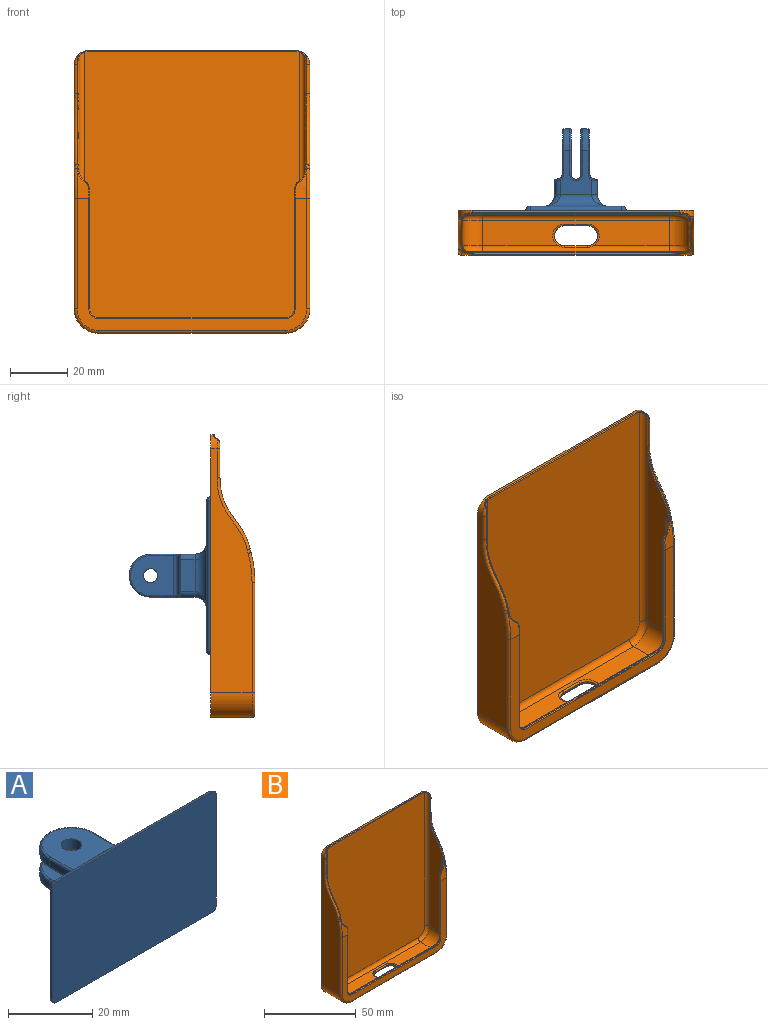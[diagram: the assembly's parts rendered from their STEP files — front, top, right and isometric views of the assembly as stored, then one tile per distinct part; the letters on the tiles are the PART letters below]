
ASSEMBLY  parts=2 mates=1
PART A: 67 faces, bbox 55x29.1x35 mm
  f0: cylinder r=1.68mm len=14mm, axis (1,0,0), area 73.7mm2, adj f13,f14,f51,f54
  f1: cylinder r=7.5mm len=15mm, axis (0,0,-1), area 47.7mm2, adj f3,f4,f43,f50
  f2: cylinder r=2.45mm len=4.9mm, axis (0,0,-1), area 46.6mm2, adj f12,f13
  f3: plane 15.5x11mm, normal (-1,0,0), area 102mm2, adj f1,f5,f26,f30,f36,f39,f41,f49
  f4: plane 15.5x11mm, normal (1,0,0), area 102mm2, adj f1,f5,f27,f32,f34,f45,f47,f52
  f5: cylinder r=7.5mm len=15mm, axis (0,0,-1), area 47.7mm2, adj f3,f4,f55,f65
  f6: cylinder r=2.45mm len=4.9mm, axis (0,0,-1), area 46.6mm2, adj f10,f14
  f7: plane 11x5mm, normal (0,0,-1), area 55mm2, adj f28,f30,f32,f44
  f8: plane 11x5mm, normal (0,0,1), area 55mm2, adj f25,f34,f36,f58
  f9: plane 12.8x0.3mm, normal (0,1,0), area 3.7mm2, adj f38,f57,f58,f60
  f10: plane 15x14mm, normal (0,0,1), area 170.1mm2, adj f6,f38,f63,f65,f66
  f11: plane 12.8x0.3mm, normal (0,1,0), area 3.7mm2, adj f37,f42,f44,f46
  f12: plane 15x14mm, normal (0,0,-1), area 170.1mm2, adj f2,f37,f41,f43,f45
  f13: plane 15.33x14mm, normal (0,0,1), area 174.7mm2, adj f0,f2,f49,f50,f52
  f14: plane 15.33x14mm, normal (0,0,-1), area 174.7mm2, adj f0,f6,f53,f55,f56
  f15: plane 55x35mm, normal (0,-1,0), area 1923.1mm2, adj f17,f18,f19,f20,f21,f22,f23,f24
  f16: plane 52x32mm, normal (0,1,0), area 1135mm2, adj f17,f18,f19,f20,f25,f26,f27,f28
  f17: cylinder r=1.5mm len=52mm, axis (1,0,0), area 122.5mm2, adj f15,f16,f21,f23
  f18: cylinder r=1.5mm len=32mm, axis (0,0,1), area 75.4mm2, adj f15,f16,f21,f22
  f19: cylinder r=1.5mm len=32mm, axis (0,0,-1), area 75.4mm2, adj f15,f16,f23,f24
  f20: cylinder r=1.5mm len=52mm, axis (-1,0,0), area 122.5mm2, adj f15,f16,f22,f24
  f21: sphere r=1.5mm, area 3.5mm2, adj f15,f17,f18
  f22: sphere r=1.5mm, area 3.5mm2, adj f15,f18,f20
  f23: sphere r=1.5mm, area 3.5mm2, adj f15,f17,f19
  f24: sphere r=1.5mm, area 3.5mm2, adj f15,f19,f20
  f25: cylinder r=4mm len=23mm, axis (-1,0,0), area 96.5mm2, adj f8,f16,f33,f35
  f26: cylinder r=4mm len=23mm, axis (0,0,1), area 96.5mm2, adj f3,f16,f29,f35
  f27: cylinder r=4mm len=23mm, axis (0,0,1), area 96.5mm2, adj f4,f16,f31,f33
  f28: cylinder r=4mm len=23mm, axis (1,0,0), area 96.5mm2, adj f7,f16,f29,f31
  f29: bspline ~6x6mm, area 14.5mm2, adj f26,f28,f30
  f30: cylinder r=2mm len=5.31mm, axis (0,1,0), area 15.9mm2, adj f3,f7,f29,f40,f42
  f31: bspline ~6x6mm, area 14.5mm2, adj f27,f28,f32
  f32: cylinder r=2mm len=5.31mm, axis (0,-1,0), area 15.9mm2, adj f4,f7,f31,f46,f48
  f33: bspline ~6x6mm, area 14.5mm2, adj f25,f27,f34
  f34: cylinder r=2mm len=5.31mm, axis (0,1,0), area 15.9mm2, adj f4,f8,f33,f60,f62
  f35: bspline ~6x6mm, area 14.5mm2, adj f25,f26,f36
  f36: cylinder r=2mm len=5.31mm, axis (0,-1,0), area 15.9mm2, adj f3,f8,f35,f57,f59
  f37: cylinder r=2mm len=14mm, axis (-1,0,0), area 43.6mm2, adj f11,f12,f39,f40,f47,f48
  f38: cylinder r=2mm len=14mm, axis (1,0,0), area 43.6mm2, adj f9,f10,f59,f61,f62,f64
  f39: torus R=2.5mm, axis (1,0,0), area 1.8mm2, adj f3,f37,f40,f41
  f40: bspline ~2.29x1.41mm, area 1.2mm2, adj f30,f37,f39,f42
  f41: cylinder r=0.5mm len=8mm, axis (0,1,0), area 6.3mm2, adj f3,f12,f39,f43
  f42: torus R=1.5mm, axis (0,1,0), area 0.9mm2, adj f11,f30,f40,f44
  f43: torus R=7mm, axis (0,0,-1), area 18.1mm2, adj f1,f12,f41,f45
  f44: cylinder r=0.5mm len=11mm, axis (1,0,0), area 8.6mm2, adj f7,f11,f42,f46
  f45: cylinder r=0.5mm len=8mm, axis (0,-1,0), area 6.3mm2, adj f4,f12,f43,f47
  f46: torus R=1.5mm, axis (0,1,0), area 0.9mm2, adj f11,f32,f44,f48
  f47: torus R=2.5mm, axis (-1,0,0), area 1.8mm2, adj f4,f37,f45,f48
  f48: bspline ~2.29x1.41mm, area 1.2mm2, adj f32,f37,f46,f47
  f49: cylinder r=0.5mm len=8.33mm, axis (0,1,0), area 6.5mm2, adj f3,f13,f50,f51
  f50: torus R=7mm, axis (0,0,1), area 18.1mm2, adj f1,f13,f49,f52
  f51: torus R=2.17mm, axis (1,0,0), area 4.6mm2, adj f0,f3,f49,f53
  f52: cylinder r=0.5mm len=8.33mm, axis (0,-1,0), area 6.5mm2, adj f4,f13,f50,f54
  f53: cylinder r=0.5mm len=8.33mm, axis (0,-1,0), area 6.5mm2, adj f3,f14,f51,f55
  f54: torus R=2.17mm, axis (-1,0,0), area 4.6mm2, adj f0,f4,f52,f56
  f55: torus R=7mm, axis (0,0,1), area 18.1mm2, adj f5,f14,f53,f56
  f56: cylinder r=0.5mm len=8.33mm, axis (0,1,0), area 6.5mm2, adj f4,f14,f54,f55
  f57: torus R=1.5mm, axis (0,-1,0), area 0.9mm2, adj f9,f36,f58,f59
  f58: cylinder r=0.5mm len=11mm, axis (1,0,0), area 8.6mm2, adj f8,f9,f57,f60
  f59: bspline ~2.29x1.41mm, area 1.2mm2, adj f36,f38,f57,f61
  f60: torus R=1.5mm, axis (0,-1,0), area 0.9mm2, adj f9,f34,f58,f62
  f61: torus R=2.5mm, axis (1,0,0), area 1.8mm2, adj f3,f38,f59,f63
  f62: bspline ~2.29x1.41mm, area 1.2mm2, adj f34,f38,f60,f64
  f63: cylinder r=0.5mm len=8mm, axis (0,1,0), area 6.3mm2, adj f3,f10,f61,f65
  f64: torus R=2.5mm, axis (-1,0,0), area 1.8mm2, adj f4,f38,f62,f66
  f65: torus R=7mm, axis (0,0,1), area 18.1mm2, adj f5,f10,f63,f66
  f66: cylinder r=0.5mm len=8mm, axis (0,-1,0), area 6.3mm2, adj f4,f10,f64,f65
PART B: 112 faces, bbox 83.6x15.8x99.4 mm
  f0: plane 72.2x0.9mm, normal (0,0,1), area 65mm2, adj f2,f46,f47,f97
  f1: plane 94.7x75mm, normal (0,-1,0), area 7091.6mm2, adj f39,f40,f41,f42,f43,f95,f97,f99
  f2: plane 98.6x82.2mm, normal (0,1,0), area 8062.4mm2, adj f0,f8,f9,f10,f11,f12,f46,f47
  f3: plane 70.95x10.57mm, normal (1,0,0), area 555.3mm2, adj f7,f38,f43,f45,f90,f92,f94
  f4: plane 65x9mm, normal (0,0,1), area 473.1mm2, adj f6,f7,f36,f41,f102,f103,f104
  f5: plane 70.95x10.57mm, normal (-1,0,0), area 555.3mm2, adj f6,f34,f39,f44,f81,f83,f85
  f6: cylinder r=7mm len=9mm, axis (0,1,0), area 99mm2, adj f4,f5,f35,f40
  f7: cylinder r=7mm len=9mm, axis (0,1,0), area 99mm2, adj f3,f4,f37,f42
  f8: plane 85x14.4mm, normal (-1,0,0), area 898.4mm2, adj f2,f9,f46,f49,f50,f51,f52,f53
  f9: cylinder r=8.6mm len=14.4mm, axis (0,1,0), area 194.5mm2, adj f2,f8,f10,f54
  f10: plane 65x14.4mm, normal (0,0,-1), area 817.6mm2, adj f2,f9,f11,f55,f108,f109,f110,f111
  f11: cylinder r=8.6mm len=14.4mm, axis (0,1,0), area 194.5mm2, adj f2,f10,f12,f56
  f12: plane 85x14.4mm, normal (1,0,0), area 898.4mm2, adj f2,f11,f47,f57,f58,f59,f60,f61
  f13: plane 11.57x0.32mm, normal (0,-1,0), area 3.5mm2, adj f14,f61,f62,f89
  f14: extruded ~24.84x10.49mm, area 8.3mm2, adj f13,f30,f60,f85,f87
  f15: plane 11.57x0.32mm, normal (0,-1,0), area 3.5mm2, adj f16,f48,f49,f98
  f16: extruded ~24.84x10.49mm, area 8.3mm2, adj f15,f31,f50,f94,f96
  f17: plane 8x0.47mm, normal (0,1,0), area 3.8mm2, adj f18,f20,f107,f111
  f18: cylinder r=3.5mm len=7mm, axis (0,0,-1), area 4.5mm2, adj f17,f19,f103,f105,f110
  f19: plane 8x0.4mm, normal (0,-1,0), area 3.2mm2, adj f18,f20,f102,f108
  f20: cylinder r=3.5mm len=7mm, axis (0,0,-1), area 4.5mm2, adj f17,f19,f104,f106,f109
  f21: plane 75x49.09mm, normal (0,1,0), area 231.2mm2, adj f34,f35,f36,f37,f38,f64,f65,f66
  f22: cylinder r=3.5mm len=2.92mm, axis (0,1,0), area 0.8mm2, adj f23,f44,f65,f77
  f23: plane 41.5x0.5mm, normal (-1,0,0), area 20.6mm2, adj f22,f24,f66,f74,f75
  f24: cylinder r=3.2mm len=3.2mm, axis (0,1,0), area 2.5mm2, adj f23,f25,f67,f76
  f25: plane 65x0.5mm, normal (0,0,1), area 32.5mm2, adj f24,f26,f68,f78
  f26: cylinder r=3.2mm len=3.2mm, axis (0,1,0), area 2.5mm2, adj f25,f27,f69,f80
  f27: plane 41.5x0.5mm, normal (1,0,0), area 20.6mm2, adj f26,f28,f70,f82,f84
  f28: cylinder r=3.5mm len=2.92mm, axis (0,1,0), area 0.8mm2, adj f27,f45,f71,f86
  f29: plane 80.2x45.99mm, normal (0,-1,0), area 652.8mm2, adj f32,f33,f53,f54,f55,f56,f57,f74
  f30: cylinder r=25mm len=1.3mm, axis (1,0,0), area 0.4mm2, adj f14,f32,f59,f83
  f31: cylinder r=25mm len=1.3mm, axis (1,0,0), area 0.4mm2, adj f16,f33,f51,f92
  f32: cylinder r=40mm len=10.47mm, axis (1,0,0), area 27.4mm2, adj f29,f30,f58,f75,f77,f79,f81
  f33: cylinder r=40mm len=10.47mm, axis (1,0,0), area 27.4mm2, adj f29,f31,f52,f84,f86,f88,f90
  f34: cylinder r=2mm len=48.58mm, axis (0,0,1), area 145.6mm2, adj f5,f21,f35,f63
  f35: torus R=5mm, axis (0,-1,0), area 31mm2, adj f6,f21,f34,f36
  f36: cylinder r=2mm len=65mm, axis (1,0,0), area 199.5mm2, adj f4,f21,f35,f37,f105,f106,f107
  f37: torus R=5mm, axis (0,-1,0), area 31mm2, adj f7,f21,f36,f38
  f38: cylinder r=2mm len=48.58mm, axis (0,0,-1), area 145.6mm2, adj f3,f21,f37,f73
  f39: cylinder r=2mm len=89.49mm, axis (0,0,-1), area 274mm2, adj f1,f5,f40,f87,f89,f91,f93
  f40: torus R=5mm, axis (0,-1,0), area 31mm2, adj f1,f6,f39,f41
  f41: cylinder r=2mm len=65mm, axis (-1,0,0), area 204.2mm2, adj f1,f4,f40,f42
  f42: torus R=5mm, axis (0,-1,0), area 31mm2, adj f1,f7,f41,f43
  f43: cylinder r=2mm len=89.49mm, axis (0,0,1), area 274mm2, adj f1,f3,f42,f96,f98,f100,f101
  f44: cylinder r=5mm len=4.17mm, axis (0,1,0), area 3mm2, adj f5,f22,f63,f64,f79
  f45: cylinder r=5mm len=4.17mm, axis (0,1,0), area 3mm2, adj f3,f28,f72,f73,f88
  f46: cylinder r=5mm len=5mm, axis (0,1,0), area 12.9mm2, adj f0,f2,f8,f48,f99,f101
  f47: cylinder r=5mm len=5mm, axis (0,-1,0), area 12.9mm2, adj f0,f2,f12,f62,f93,f95
  f48: torus R=4mm, axis (0,-1,0), area 4.2mm2, adj f15,f46,f49,f100
  f49: cylinder r=1mm len=10mm, axis (0,0,1), area 15.7mm2, adj f8,f15,f48,f50
  f50: bspline ~39.35x11.83mm, area 43.3mm2, adj f8,f16,f49,f51
  f51: torus R=26mm, axis (-1,0,0), area 2.1mm2, adj f8,f31,f50,f52
  f52: torus R=39mm, axis (-1,0,0), area 16.5mm2, adj f8,f33,f51,f53
  f53: cylinder r=1mm len=38.39mm, axis (0,0,1), area 60.3mm2, adj f8,f29,f52,f54
  f54: torus R=7.6mm, axis (0,-1,0), area 20.3mm2, adj f9,f29,f53,f55
  f55: cylinder r=1mm len=65mm, axis (-1,0,0), area 102.1mm2, adj f10,f29,f54,f56
  f56: torus R=7.6mm, axis (0,-1,0), area 20.3mm2, adj f11,f29,f55,f57
  f57: cylinder r=1mm len=38.39mm, axis (0,0,-1), area 60.3mm2, adj f12,f29,f56,f58
  f58: torus R=39mm, axis (-1,0,0), area 16.5mm2, adj f12,f32,f57,f59
  f59: torus R=26mm, axis (-1,0,0), area 2.1mm2, adj f12,f30,f58,f60
  f60: bspline ~39.35x11.83mm, area 43.3mm2, adj f12,f14,f59,f61
  f61: cylinder r=1mm len=10mm, axis (0,0,-1), area 15.7mm2, adj f12,f13,f60,f62
  f62: torus R=4mm, axis (0,-1,0), area 4.2mm2, adj f13,f47,f61,f91
  f63: bspline ~4.78x2.68mm, area 1.2mm2, adj f34,f44,f64
  f64: torus R=5.4mm, axis (0,-1,0), area 0mm2, adj f21,f44,f63,f65
  f65: torus R=3.1mm, axis (0,-1,0), area 2.1mm2, adj f21,f22,f64,f66
  f66: cylinder r=0.4mm len=41.5mm, axis (0,0,-1), area 26.1mm2, adj f21,f23,f65,f67
  f67: torus R=3.6mm, axis (0,-1,0), area 3.3mm2, adj f21,f24,f66,f68
  f68: cylinder r=0.4mm len=65mm, axis (-1,0,0), area 40.8mm2, adj f21,f25,f67,f69
  f69: torus R=3.6mm, axis (0,-1,0), area 3.3mm2, adj f21,f26,f68,f70
  f70: cylinder r=0.4mm len=41.5mm, axis (0,0,1), area 26.1mm2, adj f21,f27,f69,f71
  f71: torus R=3.1mm, axis (0,-1,0), area 2.1mm2, adj f21,f28,f70,f72
  f72: torus R=5.4mm, axis (0,-1,0), area 0mm2, adj f21,f45,f71,f73
  f73: bspline ~4.78x2.68mm, area 1.2mm2, adj f38,f45,f72
  f74: cylinder r=0.3mm len=38.39mm, axis (0,0,1), area 18.1mm2, adj f23,f29,f75,f76
  f75: torus R=39.7mm, axis (-1,0,0), area 1.5mm2, adj f23,f32,f74,f77
  f76: torus R=3.5mm, axis (0,-1,0), area 2.4mm2, adj f24,f29,f74,f78
  f77: bspline ~3.81x1.88mm, area 1.5mm2, adj f22,f32,f75,f79
  f78: cylinder r=0.3mm len=65mm, axis (1,0,0), area 30.6mm2, adj f25,f29,f76,f80
  f79: bspline ~6.24x3.52mm, area 2.3mm2, adj f32,f44,f77,f81
  f80: torus R=3.5mm, axis (0,-1,0), area 2.4mm2, adj f26,f29,f78,f82
  f81: torus R=39.7mm, axis (-1,0,0), area 0.1mm2, adj f5,f32,f79,f83
  f82: cylinder r=0.3mm len=38.39mm, axis (0,0,-1), area 18.1mm2, adj f27,f29,f80,f84
  f83: torus R=25.3mm, axis (-1,0,0), area 0.6mm2, adj f5,f30,f81,f85
  f84: torus R=39.7mm, axis (-1,0,0), area 1.5mm2, adj f27,f33,f82,f86
  f85: bspline ~22.54x10.76mm, area 11mm2, adj f5,f14,f83,f87
  f86: bspline ~4.06x2.36mm, area 1.5mm2, adj f28,f33,f84,f88
  f87: bspline ~5.25x0.67mm, area 1.8mm2, adj f14,f39,f85,f89
  f88: bspline ~5.32x3.52mm, area 2.3mm2, adj f33,f45,f86,f90
  f89: cylinder r=0.3mm len=11.57mm, axis (0,0,-1), area 5mm2, adj f13,f39,f87,f91
  f90: torus R=39.7mm, axis (-1,0,0), area 0.1mm2, adj f3,f33,f88,f92
  f91: bspline ~2.62x1.26mm, area 1.2mm2, adj f39,f62,f89,f93
  f92: torus R=25.3mm, axis (-1,0,0), area 0.6mm2, adj f3,f31,f90,f94
  f93: bspline ~2.83x1.95mm, area 1.6mm2, adj f39,f47,f91,f95
  f94: bspline ~24.06x10.99mm, area 11mm2, adj f3,f16,f92,f96
  f95: torus R=4.7mm, axis (0,-1,0), area 0.7mm2, adj f1,f47,f93,f97
  f96: bspline ~5.25x0.67mm, area 1.8mm2, adj f16,f43,f94,f98
  f97: cylinder r=0.3mm len=72.2mm, axis (1,0,0), area 34mm2, adj f0,f1,f95,f99
  f98: cylinder r=0.3mm len=11.57mm, axis (0,0,1), area 5mm2, adj f15,f43,f96,f100
  f99: torus R=4.7mm, axis (0,-1,0), area 0.7mm2, adj f1,f46,f97,f101
  f100: bspline ~2.62x1.26mm, area 1.2mm2, adj f43,f48,f98,f101
  f101: bspline ~2.83x1.95mm, area 1.6mm2, adj f43,f46,f99,f100
  f102: cylinder r=0.6mm len=8mm, axis (1,0,0), area 7.5mm2, adj f4,f19,f103,f104
  f103: torus R=4.1mm, axis (0,0,1), area 9.1mm2, adj f4,f18,f102,f105
  f104: torus R=4.1mm, axis (0,0,1), area 9.1mm2, adj f4,f20,f102,f106
  f105: bspline ~3.16x1.34mm, area 1.7mm2, adj f18,f36,f103,f107
  f106: bspline ~3.16x1.34mm, area 1.7mm2, adj f20,f36,f104,f107
  f107: cylinder r=0.6mm len=8mm, axis (1,0,0), area 6.4mm2, adj f17,f36,f105,f106
  f108: cylinder r=0.6mm len=8mm, axis (1,0,0), area 7.5mm2, adj f10,f19,f109,f110
  f109: torus R=4.1mm, axis (0,0,1), area 11mm2, adj f10,f20,f108,f111
  f110: torus R=4.1mm, axis (0,0,1), area 11mm2, adj f10,f18,f108,f111
  f111: cylinder r=0.6mm len=8mm, axis (-1,0,0), area 7.5mm2, adj f10,f17,f109,f110
PLACE A rot(axis=(0,1,0),90deg) t=(17.17,39.84,38.7)mm
PLACE B t=(-22.33,38.34,-16.62)mm fixed
MATE fastened B.f2 <-> A.f15  axis (0,1,0) through (17.17,38.34,31.2)mm
